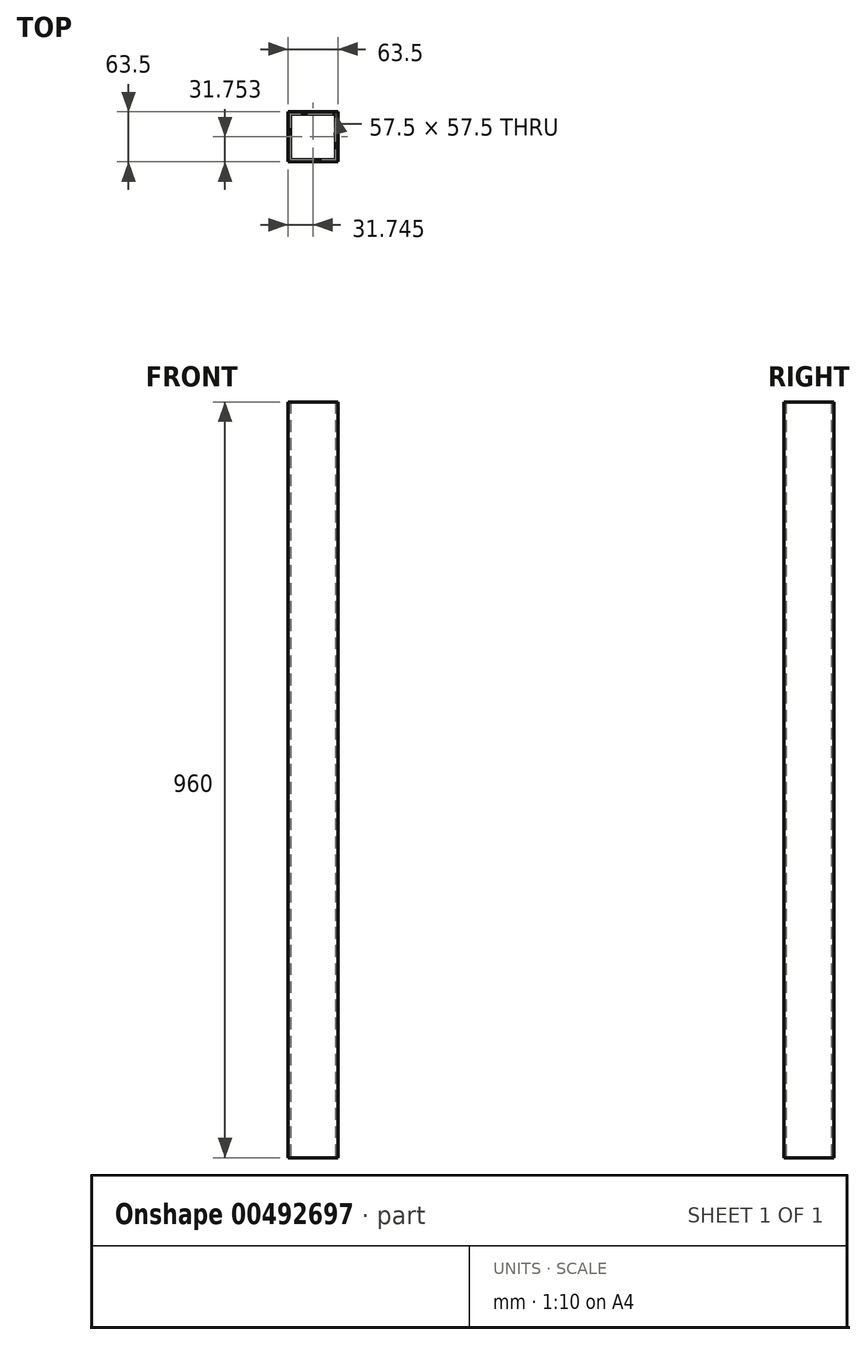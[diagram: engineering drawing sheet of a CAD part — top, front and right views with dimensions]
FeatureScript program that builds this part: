
annotation { "Feature Type Name" : "Feature", "Feature Type Description" : "" }
export const myFeature = defineFeature(function(context is Context, id is Id, definition is map)
    precondition{}
    {
        {
            var Q0;
            Q0=qCreatedBy(makeId("Top.planeOp"),FACE);
            var sketch = newSketch(context, id + "F0", { "sketchPlane" : qUnion([Q0])});
            skLineSegment(sketch, "E0.bottom", {"start": v(-36.01, 35.07) * mm, "end": v(27.49, 35.07) * mm});
            skLineSegment(sketch, "E0.top", {"start": v(-36.01, -28.43) * mm, "end": v(27.49, -28.43) * mm});
            skLineSegment(sketch, "E0.left", {"start": v(-36.01, 35.07) * mm, "end": v(-36.01, -28.43) * mm});
            skLineSegment(sketch, "E0.right", {"start": v(27.49, 35.07) * mm, "end": v(27.49, -28.43) * mm});
            skLineSegment(sketch, "E1.bottom", {"start": v(-33.01, 32.07) * mm, "end": v(24.49, 32.07) * mm});
            skLineSegment(sketch, "E1.top", {"start": v(-33.01, -25.43) * mm, "end": v(24.49, -25.43) * mm});
            skLineSegment(sketch, "E1.left", {"start": v(-33.01, 32.07) * mm, "end": v(-33.01, -25.43) * mm});
            skLineSegment(sketch, "E1.right", {"start": v(24.49, 32.07) * mm, "end": v(24.49, -25.43) * mm});
            skSolve(sketch);
        }
        {
            var Q0;
            Q0=qSketchRegion(id+"F0",true);
            extrude(context, id + "F1", {"entities" : qUnion([Q0]), "depth" : 960 * mm});
        }
    });
